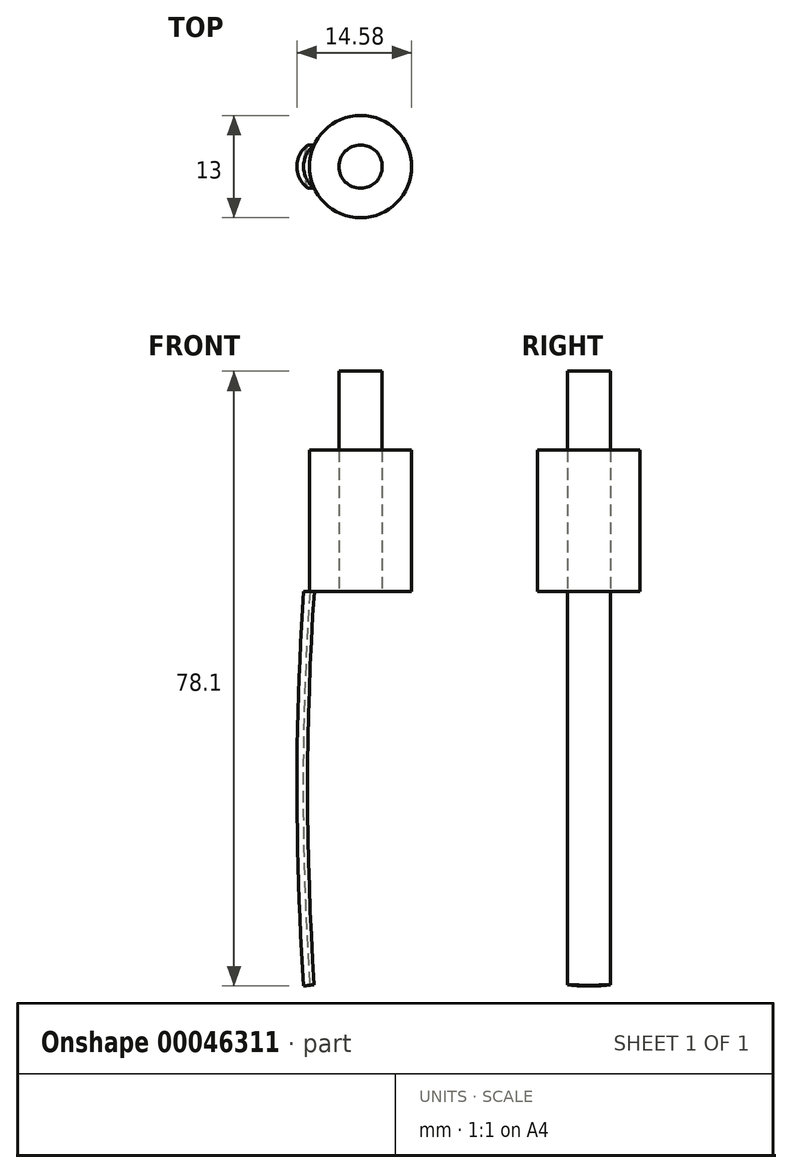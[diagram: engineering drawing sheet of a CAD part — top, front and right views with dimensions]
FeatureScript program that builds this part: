
annotation { "Feature Type Name" : "Feature", "Feature Type Description" : "" }
export const myFeature = defineFeature(function(context is Context, id is Id, definition is map)
    precondition{}
    {
        {
            var Q0;
            Q0=qCreatedBy(makeId("Top.planeOp"),FACE);
            var sketch = newSketch(context, id + "F0", { "sketchPlane" : qUnion([Q0])});
            skCircle(sketch, "E0", {"center": v(0, 0) * mm, "radius": 2.75 * mm});
            skSolve(sketch);
        }
        {
            var Q0;
            Q0=qCreatedBy(makeId("Top.planeOp"),FACE);
            var sketch = newSketch(context, id + "F1", { "sketchPlane" : qUnion([Q0])});
            skCircle(sketch, "E1", {"center": v(0, 0) * mm, "radius": 6.5 * mm});
            skSolve(sketch);
        }
        {
            var Q0;
            Q0=qCreatedBy(makeId("Top.planeOp"),FACE);
            var sketch = newSketch(context, id + "F2", { "sketchPlane" : qUnion([Q0])});
            skLineSegment(sketch, "E2", {"start": v(0, -2.75) * mm, "end": v(0, 2.75) * mm, "construction": true});
            skLineSegment(sketch, "E3", {"start": v(0, 2.75) * mm, "end": v(-5.89, 2.75) * mm, "construction": true});
            skLineSegment(sketch, "E4", {"start": v(0, -2.75) * mm, "end": v(-5.89, -2.75) * mm, "construction": true});
            skLineSegment(sketch, "E5", {"start": v(0, 0) * mm, "end": v(-6.5, 0) * mm, "construction": true});
            skSolve(sketch);
        }
        {
            var Q0;
            Q0=qCreatedBy(makeId("Top.planeOp"),FACE);
            var sketch = newSketch(context, id + "F3", { "sketchPlane" : qUnion([Q0])});
            skArc(sketch, "E6", {"start": v(-5.88, 2.73) * mm, "mid": v(-7.24, 0) * mm, "end": v(-5.88, -2.72) * mm});
            skArc(sketch, "E7", {"start": v(-5.88, 2.73) * mm, "mid": v(-6.45, 0) * mm, "end": v(-5.88, -2.72) * mm});
            skSolve(sketch);
        }
        {
            var Q0;
            Q0=qCreatedBy(makeId("Front.planeOp"),FACE);
            var sketch = newSketch(context, id + "F4", { "sketchPlane" : qUnion([Q0])});
            skLineSegment(sketch, "E8", {"start": v(-6.5, 0) * mm, "end": v(-6.5, -50) * mm});
            skArc(sketch, "E9", {"start": v(-6.5, 0) * mm, "mid": v(-7.34, -25) * mm, "end": v(-6.5, -50) * mm});
            skSolve(sketch);
        }
        {
            var Q0;
            Q0=qSketchRegion(id+"F0",true);
            extrude(context, id + "F5", {"entities" : qUnion([Q0]), "depth" : 28 * mm});
        }
        {
            var Q0;
            Q0=qSketchRegion(id+"F1",true);
            var Q1;
            Q1=sQuery(id+"F1.wireOp",EDGE,"E1");
            extrude(context, id + "F6", {"entities" : qUnion([Q0]), "surfaceEntities" : qUnion([Q1]), "depth" : 18 * mm});
        }
        {
            var Q0;
            Q0=makeQuery(id+"F3.imprint","IMPRINT",FACE,{"disambiguationData":[TD([[makeQuery(id+"F3.imprint","IMPRINT",EDGE,{"derivedFrom":sQuery(id+"F3.wireOp",EDGE,"E6")}),1.0]])]});
            var Q1;
            Q1=sQuery(id+"F3.wireOp",EDGE,"E6");
            var Q2;
            Q2=sQuery(id+"F3.wireOp",EDGE,"E7");
            var Q3;
            Q3=sQuery(id+"F4.wireOp",EDGE,"E9");
            sweep(context, id + "F7", {"profiles" : qUnion([Q0]), "surfaceProfiles" : qUnion([Q1, Q2]), "path" : qUnion([Q3])});
        }
    });
